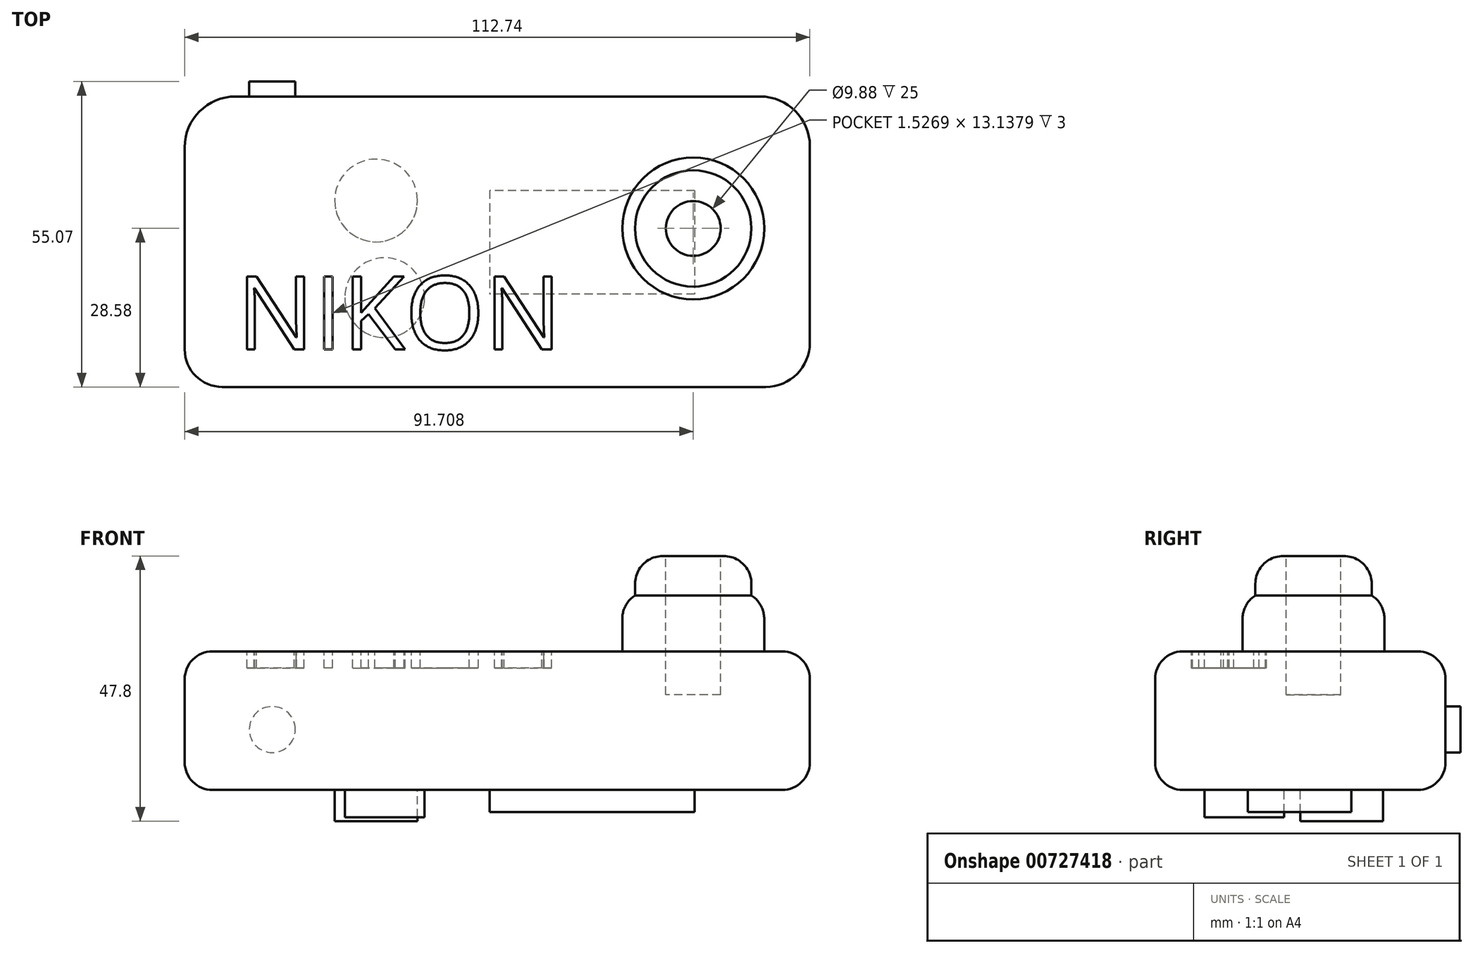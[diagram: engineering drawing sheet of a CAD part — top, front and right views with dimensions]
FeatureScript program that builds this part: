
annotation { "Feature Type Name" : "Feature", "Feature Type Description" : "" }
export const myFeature = defineFeature(function(context is Context, id is Id, definition is map)
    precondition{}
    {
        {
            var Q0;
            Q0=qCreatedBy(makeId("Top.planeOp"),FACE);
            var sketch = newSketch(context, id + "F0", { "sketchPlane" : qUnion([Q0])});
            skLineSegment(sketch, "E0.bottom", {"start": v(-59.5, 26.77) * mm, "end": v(53.24, 26.77) * mm});
            skLineSegment(sketch, "E0.top", {"start": v(-59.5, -25.6) * mm, "end": v(53.24, -25.6) * mm});
            skLineSegment(sketch, "E0.left", {"start": v(-59.5, 26.77) * mm, "end": v(-59.5, -25.6) * mm});
            skLineSegment(sketch, "E0.right", {"start": v(53.24, 26.77) * mm, "end": v(53.24, -25.6) * mm});
            skSolve(sketch);
        }
        {
            var Q0;
            Q0=makeQuery(id+"F0.imprint","IMPRINT",FACE,{"disambiguationData":[TD([[makeQuery(id+"F0.imprint","IMPRINT",EDGE,{"derivedFrom":sQuery(id+"F0.wireOp",EDGE,"E0.bottom")}),-1.0]])]});
            extrude(context, id + "F1", {"entities" : qUnion([Q0]), "depth" : 25 * mm, "offsetDistance" : 25 * mm});
        }
        {
            var Q0;
            Q0=makeQuery(id+"F1.opExtrude","CAP_FACE",FACE,{"disambiguationData":[OSD([sQuery(id+"F0.wireOp",EDGE,"E0.bottom"),sQuery(id+"F0.wireOp",EDGE,"E0.top"),sQuery(id+"F0.wireOp",EDGE,"E0.left"),sQuery(id+"F0.wireOp",EDGE,"E0.right")])],"isStart":false});
            var sketch = newSketch(context, id + "F2", { "sketchPlane" : qUnion([Q0])});
            skCircle(sketch, "E1", {"center": v(32.2, 2.98) * mm, "radius": 12.8 * mm});
            skSolve(sketch);
        }
        {
            var Q0;
            Q0 = qSketchRegion(id + "F2", true);
            extrude(context, id + "F3", {"entities" : qUnion([Q0]), "operationType" : NewBodyOperationType.ADD, "depth" : 10.1 * mm, "offsetDistance" : 25 * mm});
        }
        {
            var Q0;
            Q0=makeQuery(id+"F3.opExtrude","CAP_FACE",FACE,{"disambiguationData":[OSD([sQuery(id+"F2.wireOp",EDGE,"E1")])],"isStart":false});
            var sketch = newSketch(context, id + "F4", { "sketchPlane" : qUnion([Q0])});
            skCircle(sketch, "E2", {"center": v(32.2, 2.98) * mm, "radius": 10.49 * mm});
            skSolve(sketch);
        }
        {
            var Q0;
            Q0=makeQuery(id+"F4.imprint","IMPRINT",FACE,{"disambiguationData":[TD([[makeQuery(id+"F4.imprint","IMPRINT",EDGE,{"derivedFrom":sQuery(id+"F4.wireOp",EDGE,"E2")}),1.0]])]});
            extrude(context, id + "F5", {"entities" : qUnion([Q0]), "operationType" : NewBodyOperationType.ADD, "depth" : 7.1 * mm, "offsetDistance" : 25 * mm});
        }
        {
            var Q0;
            Q0=makeQuery(id+"F5.opExtrude","CAP_FACE",FACE,{"disambiguationData":[OSD([sQuery(id+"F4.wireOp",EDGE,"E2")])],"isStart":false});
            var sketch = newSketch(context, id + "F6", { "sketchPlane" : qUnion([Q0])});
            skCircle(sketch, "E3", {"center": v(32.2, 2.98) * mm, "radius": 6.24 * mm});
            skSolve(sketch);
        }
        {
            var Q0;
            Q0=makeQuery(id+"F6.imprint","IMPRINT",FACE,{"disambiguationData":[TD([[makeQuery(id+"F6.imprint","IMPRINT",EDGE,{"derivedFrom":sQuery(id+"F6.wireOp",EDGE,"E3")}),1.0]])]});
            extrude(context, id + "F7", {"entities" : qUnion([Q0]), "operationType" : NewBodyOperationType.ADD, "oppositeDirection" : true, "depth" : 6.3 * mm, "offsetDistance" : 25 * mm});
        }
        {
            var Q0;
            Q0=makeQuery(id+"F5.opExtrude","CAP_FACE",FACE,{"disambiguationData":[OSD([sQuery(id+"F4.wireOp",EDGE,"E2")])],"isStart":false});
            var sketch = newSketch(context, id + "F8", { "sketchPlane" : qUnion([Q0])});
            skCircle(sketch, "E4", {"center": v(32.2, 2.98) * mm, "radius": 5.53 * mm});
            skSolve(sketch);
        }
        {
            var Q0;
            Q0=makeQuery(id+"F8.imprint","IMPRINT",FACE,{"disambiguationData":[TD([[makeQuery(id+"F8.imprint","IMPRINT",EDGE,{"derivedFrom":sQuery(id+"F8.wireOp",EDGE,"E4")}),1.0]])]});
            extrude(context, id + "F9", {"entities" : qUnion([Q0]), "operationType" : NewBodyOperationType.ADD, "oppositeDirection" : true, "depth" : 6.8 * mm, "offsetDistance" : 25 * mm});
        }
        {
            var Q0;
            Q0=makeQuery(id+"F5.opExtrude","CAP_FACE",FACE,{"disambiguationData":[OSD([sQuery(id+"F4.wireOp",EDGE,"E2")])],"isStart":false});
            var sketch = newSketch(context, id + "F10", { "sketchPlane" : qUnion([Q0])});
            skCircle(sketch, "E5", {"center": v(32.2, 2.98) * mm, "radius": 4.94 * mm});
            skSolve(sketch);
        }
        {
            var Q0;
            Q0 = qSketchRegion(id + "F10", true);
            extrude(context, id + "F11", {"entities" : qUnion([Q0]), "operationType" : NewBodyOperationType.REMOVE, "oppositeDirection" : true, "depth" : 25 * mm, "offsetDistance" : 25 * mm});
        }
        {
            var Q0;
            Q0=makeQuery(id+"F1.opExtrude","SWEPT_EDGE",EDGE,{"disambiguationData":[OSD([sQuery(id+"F0.wireOp",EDGE,"E0.bottom"),sQuery(id+"F0.wireOp",EDGE,"E0.left")])]});
            fillet(context, id + "F12", {"entities" : qUnion([Q0]), "radius" : 9.17 * mm, "tangentPropagation" : true, "allowEdgeOverflow" : false});
        }
        {
            var Q0;
            Q0=makeQuery(id+"F1.opExtrude","SWEPT_EDGE",EDGE,{"disambiguationData":[OSD([sQuery(id+"F0.wireOp",EDGE,"E0.bottom"),sQuery(id+"F0.wireOp",EDGE,"E0.right")])]});
            fillet(context, id + "F13", {"entities" : qUnion([Q0]), "radius" : 8.93 * mm, "tangentPropagation" : true, "allowEdgeOverflow" : false});
        }
        {
            var Q0;
            Q0=makeQuery(id+"F1.opExtrude","SWEPT_EDGE",EDGE,{"disambiguationData":[OSD([sQuery(id+"F0.wireOp",EDGE,"E0.top"),sQuery(id+"F0.wireOp",EDGE,"E0.right")])]});
            fillet(context, id + "F14", {"entities" : qUnion([Q0]), "radius" : 7.97 * mm, "tangentPropagation" : true, "allowEdgeOverflow" : false});
        }
        {
            var Q0;
            Q0=makeQuery(id+"F1.opExtrude","SWEPT_EDGE",EDGE,{"disambiguationData":[OSD([sQuery(id+"F0.wireOp",EDGE,"E0.top"),sQuery(id+"F0.wireOp",EDGE,"E0.left")])]});
            fillet(context, id + "F15", {"entities" : qUnion([Q0]), "radius" : 6.76 * mm, "tangentPropagation" : true, "allowEdgeOverflow" : false});
        }
        {
            var Q0;
            Q0=makeQuery(id+"F1.opExtrude","SWEPT_FACE",FACE,{"disambiguationData":[OSD([sQuery(id+"F0.wireOp",EDGE,"E0.bottom")])]});
            var sketch = newSketch(context, id + "F16", { "sketchPlane" : qUnion([Q0])});
            skCircle(sketch, "E6", {"center": v(43.7, 10.9) * mm, "radius": 4.15 * mm});
            skSolve(sketch);
        }
        {
            var Q0;
            Q0=makeQuery(id+"F16.imprint","IMPRINT",FACE,{"disambiguationData":[TD([[makeQuery(id+"F16.imprint","IMPRINT",EDGE,{"derivedFrom":sQuery(id+"F16.wireOp",EDGE,"E6")}),1.0]])]});
            extrude(context, id + "F17", {"entities" : qUnion([Q0]), "operationType" : NewBodyOperationType.ADD, "depth" : 2.7 * mm, "offsetDistance" : 25 * mm});
        }
        {
            var Q0;
            Q0=makeQuery(id+"F3.opExtrude","CAP_EDGE",EDGE,{"disambiguationData":[OSD([sQuery(id+"F2.wireOp",EDGE,"E1")])],"isStart":false});
            fillet(context, id + "F18", {"entities" : qUnion([Q0]), "radius" : 5 * mm, "tangentPropagation" : true, "allowEdgeOverflow" : false});
        }
        {
            var Q0;
            Q0=makeQuery(id+"F5.opExtrude","CAP_EDGE",EDGE,{"disambiguationData":[OSD([sQuery(id+"F4.wireOp",EDGE,"E2")])],"isStart":false});
            fillet(context, id + "F19", {"entities" : qUnion([Q0]), "radius" : 5 * mm, "tangentPropagation" : true, "allowEdgeOverflow" : false});
        }
        {
            var Q0;
            Q0=makeQuery(id+"F1.opExtrude","CAP_FACE",FACE,{"disambiguationData":[OSD([sQuery(id+"F0.wireOp",EDGE,"E0.bottom"),sQuery(id+"F0.wireOp",EDGE,"E0.top"),sQuery(id+"F0.wireOp",EDGE,"E0.left"),sQuery(id+"F0.wireOp",EDGE,"E0.right")])],"isStart":true});
            var sketch = newSketch(context, id + "F20", { "sketchPlane" : qUnion([Q0])});
            skLineSegment(sketch, "E7.bottom", {"start": v(32.47, -9.82) * mm, "end": v(-4.51, -9.82) * mm});
            skLineSegment(sketch, "E7.top", {"start": v(32.47, 8.84) * mm, "end": v(-4.51, 8.84) * mm});
            skLineSegment(sketch, "E7.left", {"start": v(32.47, -9.82) * mm, "end": v(32.47, 8.84) * mm});
            skLineSegment(sketch, "E7.right", {"start": v(-4.51, -9.82) * mm, "end": v(-4.51, 8.84) * mm});
            skSolve(sketch);
        }
        {
            var Q0;
            Q0=makeQuery(id+"F20.imprint","IMPRINT",FACE,{"disambiguationData":[TD([[makeQuery(id+"F20.imprint","IMPRINT",EDGE,{"derivedFrom":sQuery(id+"F20.wireOp",EDGE,"E7.bottom")}),-1.0]])]});
            extrude(context, id + "F21", {"entities" : qUnion([Q0]), "operationType" : NewBodyOperationType.ADD, "depth" : 4 * mm, "offsetDistance" : 25 * mm});
        }
        {
            var Q0;
            Q0=makeQuery(id+"F1.opExtrude","CAP_EDGE",EDGE,{"disambiguationData":[OSD([sQuery(id+"F0.wireOp",EDGE,"E0.bottom")])],"isStart":false});
            fillet(context, id + "F22", {"entities" : qUnion([Q0]), "radius" : 5 * mm, "tangentPropagation" : true, "allowEdgeOverflow" : false});
        }
        {
            var Q0;
            Q0=makeQuery(id+"F1.opExtrude","CAP_EDGE",EDGE,{"disambiguationData":[OSD([sQuery(id+"F0.wireOp",EDGE,"E0.bottom")])],"isStart":true});
            fillet(context, id + "F23", {"entities" : qUnion([Q0]), "radius" : 5 * mm, "tangentPropagation" : true, "allowEdgeOverflow" : false});
        }
        {
            var Q0;
            Q0=makeQuery(id+"F1.opExtrude","CAP_FACE",FACE,{"disambiguationData":[OSD([sQuery(id+"F0.wireOp",EDGE,"E0.bottom"),sQuery(id+"F0.wireOp",EDGE,"E0.top"),sQuery(id+"F0.wireOp",EDGE,"E0.left"),sQuery(id+"F0.wireOp",EDGE,"E0.right")])],"isStart":false});
            var sketch = newSketch(context, id + "F24", { "sketchPlane" : qUnion([Q0])});
            skText(sketch, "E8", { "text": "NIKON", "fontName": "OpenSans-Regular.ttf"});
            const initialGuessF24  = {"E8": [-0.05005, -0.01884, 1, 0, 0.01325]};
            skSetInitialGuess(sketch, initialGuessF24);
            skSolve(sketch);
        }
        {
            var Q0;
            Q0 = qSketchRegion(id + "F24", true);
            extrude(context, id + "F25", {"entities" : qUnion([Q0]), "operationType" : NewBodyOperationType.REMOVE, "oppositeDirection" : true, "depth" : 3 * mm, "offsetDistance" : 25 * mm});
        }
        {
            var Q0;
            {var subQ0=sQuery(id+"F0.wireOp",EDGE,"E0.left");var subQ1=sQuery(id+"F0.wireOp",EDGE,"E0.top");var subQ2=sQuery(id+"F0.wireOp",EDGE,"E0.right");var subQ3=sQuery(id+"F0.wireOp",EDGE,"E0.bottom");var subQ4=makeQuery(id+"F1.opExtrude","CAP_FACE",FACE,{"disambiguationData":[OSD([subQ3,subQ1,subQ0,subQ2])],"isStart":true});var subQ5=subQ4;var subQ6=subQ5;var subQ7=subQ6;Q0=makeQuery(id+"Fh1wCjNvQBECTC8_1.boolean.opBoolean","SPLIT",FACE,{"disambiguationData":[TD([makeQuery(id+"F21.opExtrude","SWEPT_FACE",FACE,{"disambiguationData":[OSD([sQuery(id+"F20.wireOp",EDGE,"E7.bottom")])]})])],"derivedFrom":subQ7});}
            var sketch = newSketch(context, id + "F26", { "sketchPlane" : qUnion([Q0])});
            skCircle(sketch, "E9", {"center": v(-24.99, -8.02) * mm, "radius": 7.46 * mm});
            skSolve(sketch);
        }
        {
            var Q0;
            Q0 = qSketchRegion(id + "F26", true);
            extrude(context, id + "F27", {"entities" : qUnion([Q0]), "operationType" : NewBodyOperationType.ADD, "depth" : 5.6 * mm, "offsetDistance" : 25 * mm});
        }
        {
            var Q0;
            {var subQ0=sQuery(id+"F0.wireOp",EDGE,"E0.left");var subQ1=sQuery(id+"F0.wireOp",EDGE,"E0.top");var subQ2=sQuery(id+"F0.wireOp",EDGE,"E0.right");var subQ3=sQuery(id+"F0.wireOp",EDGE,"E0.bottom");var subQ4=makeQuery(id+"F1.opExtrude","CAP_FACE",FACE,{"disambiguationData":[OSD([subQ3,subQ1,subQ0,subQ2])],"isStart":true});var subQ5=subQ4;var subQ6=subQ5;var subQ7=subQ6;Q0=makeQuery(id+"Fh1wCjNvQBECTC8_1.boolean.opBoolean","SPLIT",FACE,{"disambiguationData":[TD([makeQuery(id+"F21.opExtrude","SWEPT_FACE",FACE,{"disambiguationData":[OSD([sQuery(id+"F20.wireOp",EDGE,"E7.bottom")])]})])],"derivedFrom":subQ7});}
            var sketch = newSketch(context, id + "F28", { "sketchPlane" : qUnion([Q0])});
            skCircle(sketch, "E10", {"center": v(-23.44, 9.51) * mm, "radius": 7.2 * mm});
            skSolve(sketch);
        }
        {
            var Q0;
            Q0 = qSketchRegion(id + "F28", true);
            extrude(context, id + "F29", {"entities" : qUnion([Q0]), "operationType" : NewBodyOperationType.ADD, "depth" : 4.9 * mm, "offsetDistance" : 25 * mm});
        }
    });
